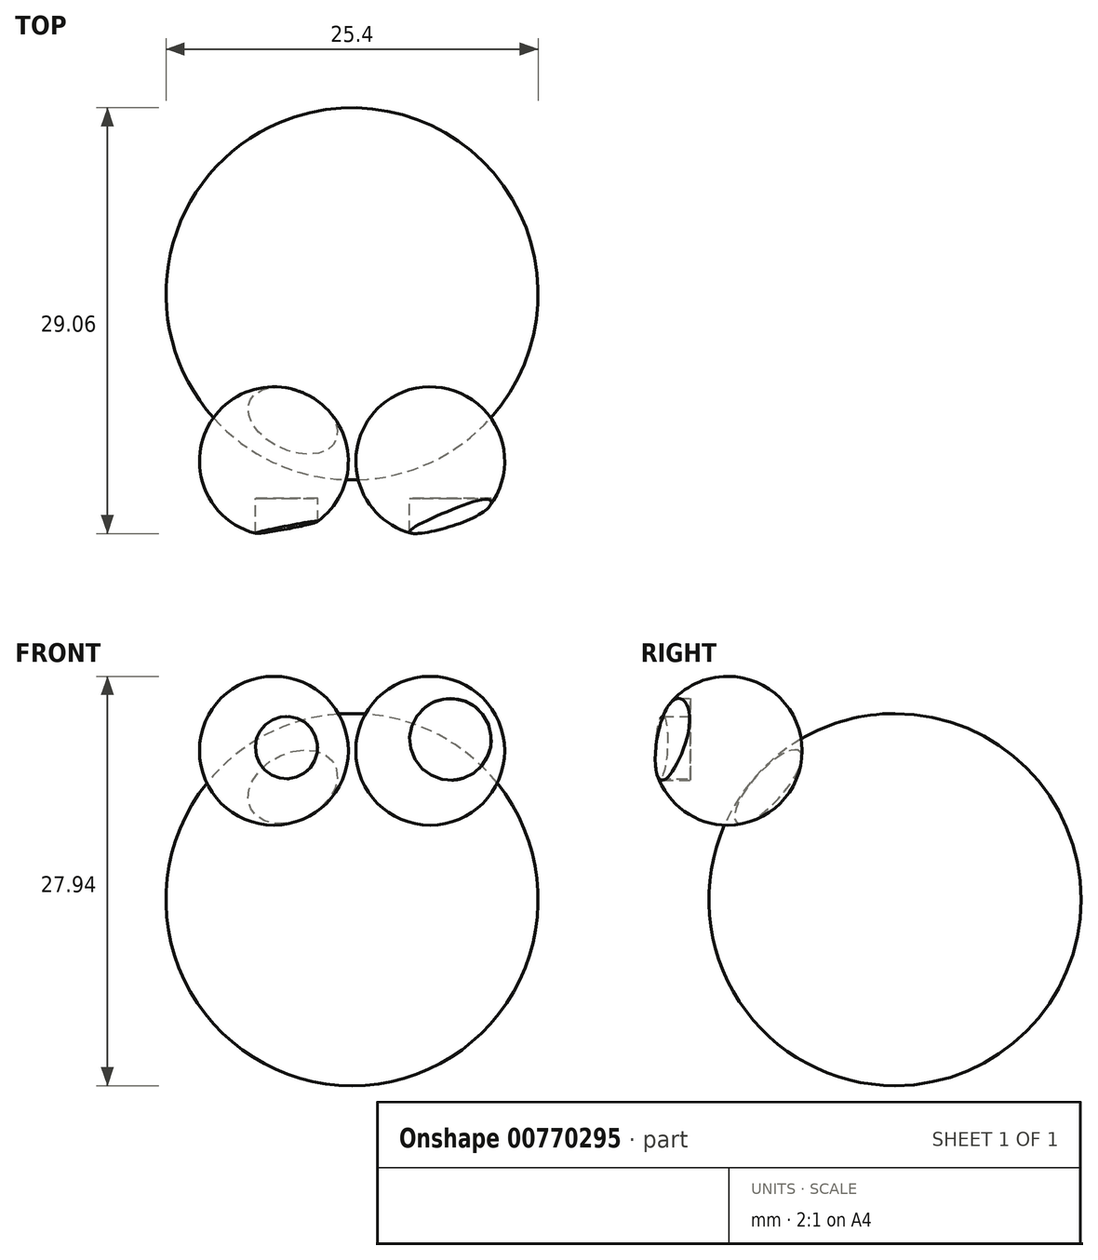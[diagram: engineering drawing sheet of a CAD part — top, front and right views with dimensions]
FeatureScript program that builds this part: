
annotation { "Feature Type Name" : "Feature", "Feature Type Description" : "" }
export const myFeature = defineFeature(function(context is Context, id is Id, definition is map)
    precondition{}
    {
        {
            var Q0;
            Q0=qCreatedBy(makeId("Top.planeOp"),FACE);
            var sketch = newSketch(context, id + "F0", { "sketchPlane" : qUnion([Q0])});
            skCircle(sketch, "E0", {"center": v(0, 0) * mm, "radius": 12.7 * mm});
            skSolve(sketch);
        }
        {
            var Q0;
            Q0 = qSketchRegion(id + "F0", true);
            extrude(context, id + "F1", {"entities" : qUnion([Q0]), "depth" : 25.4 * mm, "offsetDistance" : 25.4 * mm});
        }
        {
            var Q0;
            Q0=makeQuery(id+"F1.opExtrude","CAP_EDGE",EDGE,{"disambiguationData":[OSD([sQuery(id+"F0.wireOp",EDGE,"E0")])],"isStart":false});
            var Q1;
            Q1=makeQuery(id+"F1.opExtrude","CAP_EDGE",EDGE,{"disambiguationData":[OSD([sQuery(id+"F0.wireOp",EDGE,"E0")])],"isStart":true});
            fillet(context, id + "F2", {"entities" : qUnion([Q0, Q1]), "radius" : 12.7 * mm, "tangentPropagation" : true, "allowEdgeOverflow" : false});
        }
        {
            var Q0;
            Q0=qCreatedBy(makeId("Top.planeOp"),FACE);
            cPlane(context, id + "F3", {"entities" : qUnion([Q0]), "cplaneType" : CPlaneType.OFFSET, "offset" : 17.78 * mm, "width" : 152.4 * mm, "height" : 152.4 * mm});
        }
        {
            var Q0;
            Q0=qCreatedBy(id+"F3.planeOp",FACE);
            var sketch = newSketch(context, id + "F4", { "sketchPlane" : qUnion([Q0])});
            skCircle(sketch, "E1", {"center": v(-5.33, -11.43) * mm, "radius": 5.08 * mm});
            skSolve(sketch);
        }
        {
            var Q0;
            Q0 = qSketchRegion(id + "F4", true);
            extrude(context, id + "F5", {"entities" : qUnion([Q0]), "operationType" : NewBodyOperationType.ADD, "depth" : 10.16 * mm, "offsetDistance" : 25.4 * mm});
        }
        {
            var Q0;
            Q0=makeQuery(id+"F5.opExtrude","CAP_EDGE",EDGE,{"disambiguationData":[OSD([sQuery(id+"F4.wireOp",EDGE,"E1")])],"isStart":false});
            var Q1;
            Q1=makeQuery(id+"F5.opExtrude","CAP_EDGE",EDGE,{"disambiguationData":[OSD([sQuery(id+"F4.wireOp",EDGE,"E1")])],"isStart":true});
            fillet(context, id + "F6", {"entities" : qUnion([Q0, Q1]), "radius" : 5.08 * mm, "tangentPropagation" : true, "allowEdgeOverflow" : false});
        }
        {
            var Q0;
            Q0=qCreatedBy(makeId("Front.planeOp"),FACE);
            cPlane(context, id + "F7", {"entities" : qUnion([Q0]), "cplaneType" : CPlaneType.OFFSET, "offset" : 13.97 * mm, "width" : 152.4 * mm, "height" : 152.4 * mm});
        }
        {
            var Q0;
            Q0=qCreatedBy(id+"F7.planeOp",FACE);
            var sketch = newSketch(context, id + "F8", { "sketchPlane" : qUnion([Q0])});
            skCircle(sketch, "E2", {"center": v(-4.48, 23.08) * mm, "radius": 2.13 * mm});
            skSolve(sketch);
        }
        {
            var Q0;
            Q0 = qSketchRegion(id + "F8", true);
            extrude(context, id + "F9", {"entities" : qUnion([Q0]), "operationType" : NewBodyOperationType.REMOVE, "depth" : 3.07 * mm, "offsetDistance" : 25.4 * mm});
        }
        {
            var Q0;
            Q0=qCreatedBy(id+"F3.planeOp",FACE);
            var sketch = newSketch(context, id + "F10", { "sketchPlane" : qUnion([Q0])});
            skCircle(sketch, "E3", {"center": v(5.33, -11.43) * mm, "radius": 5.08 * mm});
            skSolve(sketch);
        }
        {
            var Q0;
            Q0=makeQuery(id+"F10.imprint","IMPRINT",FACE,{"disambiguationData":[TD([[makeQuery(id+"F10.imprint","IMPRINT",EDGE,{"derivedFrom":sQuery(id+"F10.wireOp",EDGE,"E3")}),1.0]])]});
            var Q1;
            Q1=sQuery(id+"F10.wireOp",EDGE,"E3");
            extrude(context, id + "F11", {"entities" : qUnion([Q0]), "surfaceOperationType" : NewSurfaceOperationType.ADD, "surfaceEntities" : qUnion([Q1]), "depth" : 10.16 * mm, "offsetDistance" : 25.4 * mm});
        }
        {
            var Q0;
            Q0=makeQuery(id+"F11.opExtrude","CAP_EDGE",EDGE,{"disambiguationData":[OSD([sQuery(id+"F10.wireOp",EDGE,"E3")])],"isStart":true});
            var Q1;
            Q1=makeQuery(id+"F11.opExtrude","CAP_EDGE",EDGE,{"disambiguationData":[OSD([sQuery(id+"F10.wireOp",EDGE,"E3")])],"isStart":false});
            fillet(context, id + "F12", {"entities" : qUnion([Q0, Q1]), "radius" : 5.08 * mm, "tangentPropagation" : true, "allowEdgeOverflow" : false});
        }
        {
            var Q0;
            Q0=qCreatedBy(id+"F7.planeOp",FACE);
            var sketch = newSketch(context, id + "F13", { "sketchPlane" : qUnion([Q0])});
            skCircle(sketch, "E4", {"center": v(6.71, 23.64) * mm, "radius": 2.79 * mm});
            skSolve(sketch);
        }
        {
            var Q0;
            Q0 = qSketchRegion(id + "F13", true);
            extrude(context, id + "F14", {"entities" : qUnion([Q0]), "operationType" : NewBodyOperationType.REMOVE, "depth" : 25.4 * mm, "offsetDistance" : 25.4 * mm});
        }
    });
